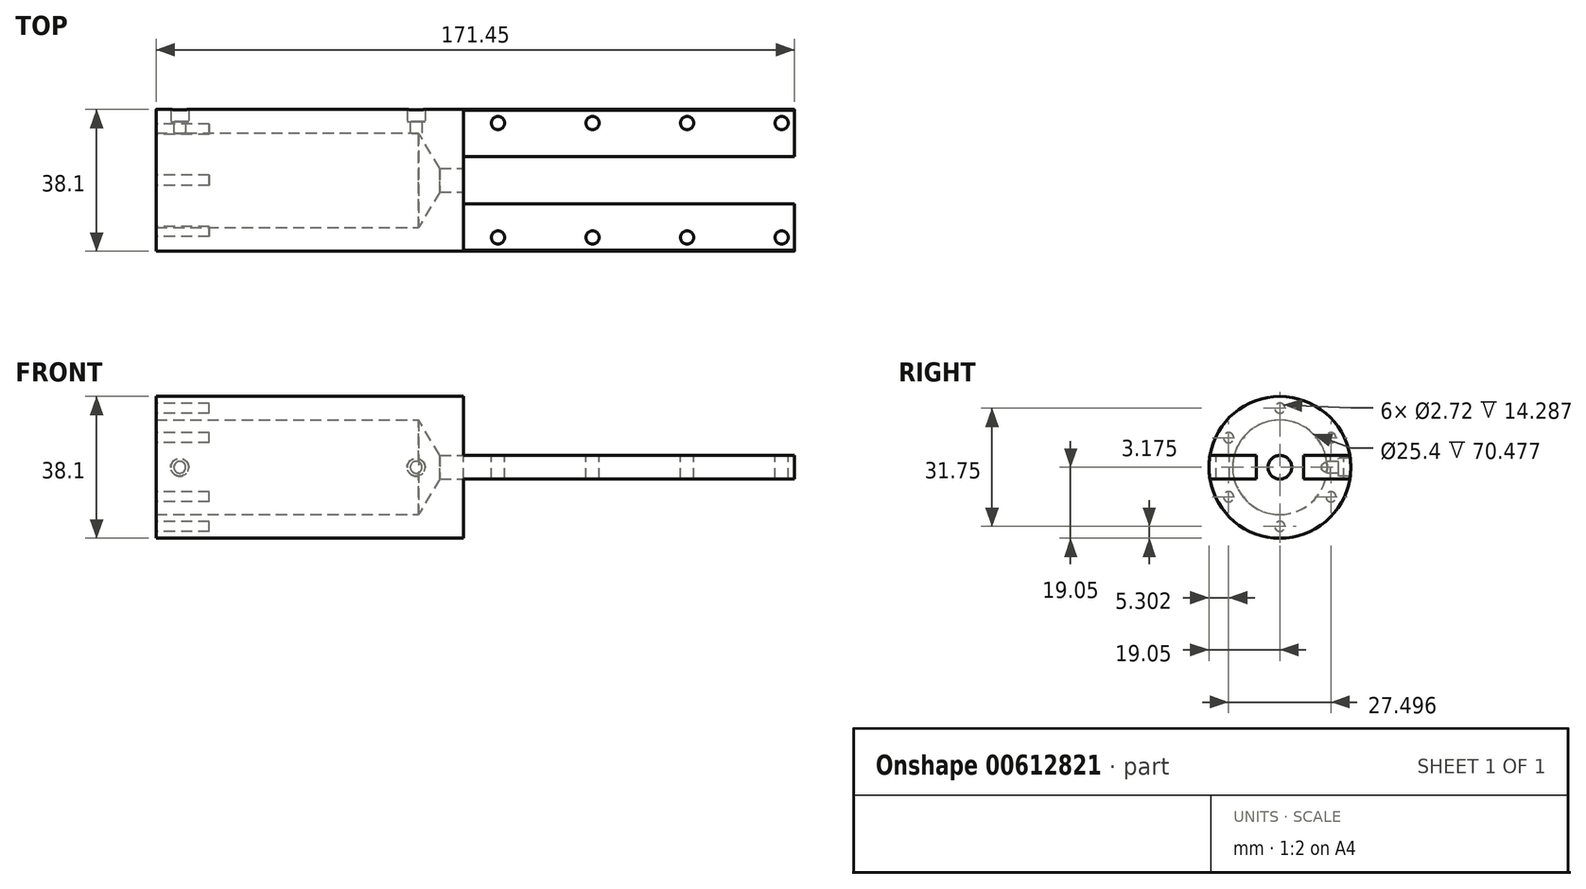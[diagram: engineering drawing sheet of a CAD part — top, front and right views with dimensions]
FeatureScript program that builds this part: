
annotation { "Feature Type Name" : "Feature", "Feature Type Description" : "" }
export const myFeature = defineFeature(function(context is Context, id is Id, definition is map)
    precondition{}
    {
        {
            var Q0;
            Q0=qCreatedBy(makeId("Right.planeOp"),FACE);
            var sketch = newSketch(context, id + "F0", { "sketchPlane" : qUnion([Q0])});
            skCircle(sketch, "E0", {"center": v(0, 0) * mm, "radius": 19.05 * mm});
            skSolve(sketch);
        }
        {
            var Q0;
            Q0=qSketchRegion(id+"F0",true);
            extrude(context, id + "F1", {"entities" : qUnion([Q0]), "depth" : 171.45 * mm});
        }
        {
            var Q0;
            Q0=qCreatedBy(makeId("Front.planeOp"),FACE);
            var sketch = newSketch(context, id + "F2", { "sketchPlane" : qUnion([Q0])});
            skLineSegment(sketch, "E1.bottom", {"start": v(82.55, 3.18) * mm, "end": v(171.45, 3.18) * mm});
            skLineSegment(sketch, "E1.top", {"start": v(82.55, 19.05) * mm, "end": v(171.45, 19.05) * mm});
            skLineSegment(sketch, "E1.left", {"start": v(82.55, 3.18) * mm, "end": v(82.55, 19.05) * mm});
            skLineSegment(sketch, "E1.right", {"start": v(171.45, 3.18) * mm, "end": v(171.45, 19.05) * mm});
            skLineSegment(sketch, "E2.bottom", {"start": v(82.55, -3.18) * mm, "end": v(171.45, -3.18) * mm});
            skLineSegment(sketch, "E2.top", {"start": v(82.55, -19.05) * mm, "end": v(171.45, -19.05) * mm});
            skLineSegment(sketch, "E2.left", {"start": v(82.55, -3.18) * mm, "end": v(82.55, -19.05) * mm});
            skLineSegment(sketch, "E2.right", {"start": v(171.45, -3.18) * mm, "end": v(171.45, -19.05) * mm});
            skLineSegment(sketch, "E3", {"start": v(0, 19.05) * mm, "end": v(171.45, 19.05) * mm, "construction": true});
            skLineSegment(sketch, "E4", {"start": v(171.45, -19.05) * mm, "end": v(0, -19.05) * mm, "construction": true});
            skSolve(sketch);
        }
        {
            var Q0;
            Q0=qSketchRegion(id+"F2",true);
            extrude(context, id + "F3", {"entities" : qUnion([Q0]), "operationType" : NewBodyOperationType.REMOVE, "oppositeDirection" : true, "depth" : 50.8 * mm, "symmetric" : true});
        }
        {
            var Q0;
            Q0=qCreatedBy(makeId("Top.planeOp"),FACE);
            var sketch = newSketch(context, id + "F4", { "sketchPlane" : qUnion([Q0])});
            skLineSegment(sketch, "E5.bottom", {"start": v(171.45, 6.35) * mm, "end": v(82.55, 6.35) * mm});
            skLineSegment(sketch, "E5.top", {"start": v(171.45, -6.35) * mm, "end": v(82.55, -6.35) * mm});
            skLineSegment(sketch, "E5.left", {"start": v(171.45, 6.35) * mm, "end": v(171.45, -6.35) * mm});
            skLineSegment(sketch, "E5.right", {"start": v(82.55, 6.35) * mm, "end": v(82.55, -6.35) * mm});
            skCircle(sketch, "E6", {"center": v(91.82, 15.37) * mm, "radius": 1.78 * mm});
            skCircle(sketch, "E7", {"center": v(91.82, -15.37) * mm, "radius": 1.78 * mm});
            skCircle(sketch, "E8.1.0.0", {"center": v(117.22, 15.37) * mm, "radius": 1.78 * mm});
            skCircle(sketch, "E8.1.0.1", {"center": v(117.22, -15.37) * mm, "radius": 1.78 * mm});
            skCircle(sketch, "E8.2.0.0", {"center": v(142.62, 15.37) * mm, "radius": 1.78 * mm});
            skCircle(sketch, "E8.2.0.1", {"center": v(142.62, -15.37) * mm, "radius": 1.78 * mm});
            skCircle(sketch, "E8.3.0.0", {"center": v(168.02, 15.37) * mm, "radius": 1.78 * mm});
            skCircle(sketch, "E8.3.0.1", {"center": v(168.02, -15.37) * mm, "radius": 1.78 * mm});
            skLineSegment(sketch, "E8.direction1", {"start": v(91.82, 15.37) * mm, "end": v(117.22, 15.37) * mm, "construction": true});
            skSolve(sketch);
        }
        {
            var Q0;
            Q0=qSketchRegion(id+"F4",true);
            extrude(context, id + "F5", {"entities" : qUnion([Q0]), "operationType" : NewBodyOperationType.REMOVE, "oppositeDirection" : true, "depth" : 50.8 * mm, "symmetric" : true});
        }
        {
            var Q0;
            Q0=qCreatedBy(makeId("Top.planeOp"),FACE);
            var sketch = newSketch(context, id + "F6", { "sketchPlane" : qUnion([Q0])});
            skLineSegment(sketch, "E9", {"start": v(0, 0) * mm, "end": v(82.55, 0) * mm});
            skLineSegment(sketch, "E10", {"start": v(82.55, 0) * mm, "end": v(82.55, 3.18) * mm});
            skLineSegment(sketch, "E11", {"start": v(82.55, 3.18) * mm, "end": v(76.2, 3.18) * mm});
            skLineSegment(sketch, "E12", {"start": v(76.2, 3.18) * mm, "end": v(70.48, 12.7) * mm});
            skLineSegment(sketch, "E13", {"start": v(70.48, 12.7) * mm, "end": v(0, 12.7) * mm});
            skLineSegment(sketch, "E14", {"start": v(0, 12.7) * mm, "end": v(0, 0) * mm});
            skSolve(sketch);
        }
        {
            var Q0;
            Q0=qSketchRegion(id+"F6",true);
            var Q1;
            Q1=sQuery(id+"F6.wireOp",EDGE,"E9");
            revolve(context, id + "F7", {"operationType" : NewBodyOperationType.REMOVE, "entities" : qUnion([Q0]), "axis" : qUnion([Q1]), "revolveType" : RevolveType.FULL, "oppositeDirection" : true});
        }
        {
            var Q0;
            Q0=qCreatedBy(makeId("Front.planeOp"),FACE);
            cPlane(context, id + "F8", {"entities" : qUnion([Q0]), "cplaneType" : CPlaneType.OFFSET, "offset" : 19.05 * mm, "oppositeDirection" : true, "width" : 152.4 * mm, "height" : 152.4 * mm});
        }
        {
            var Q0;
            Q0=qCreatedBy(id+"F8.planeOp",FACE);
            var sketch = newSketch(context, id + "F9", { "sketchPlane" : qUnion([Q0])});
            skPoint(sketch, "E15", {"position": v(6.35, 0) * mm});
            skPoint(sketch, "E16", {"position": v(69.85, 0) * mm});
            skSolve(sketch);
        }
        {
            var Q0;
            Q0=sQuery(id+"F9.wireOp",VERTEX,"E15");
            var Q1;
            Q1=sQuery(id+"F9.wireOp",VERTEX,"E16");
            var Q2;
            Q2=makeQuery(id+"F1.opExtrude","SWEPT_BODY",BODY,{"disambiguationData":[OSD([sQuery(id+"F0.wireOp",EDGE,"E0")])]});
            hole(context, id + "F10", {"style" : HoleStyle.C_BORE, "holeDiameter" : 3.17 * mm, "cBoreDiameter" : 4.78 * mm, "cBoreDepth" : 3.17 * mm, "endStyle" : HoleEndStyle.BLIND, "oppositeDirection" : true, "holeDepth" : 7.62 * mm, "locations" : qUnion([Q0, Q1]), "scope" : qUnion([Q2])});
        }
        {
            var Q0;
            Q0=qCreatedBy(makeId("Right.planeOp"),FACE);
            var sketch = newSketch(context, id + "F11", { "sketchPlane" : qUnion([Q0])});
            skCircle(sketch, "E17", {"center": v(0, 0) * mm, "radius": 15.88 * mm, "construction": true});
            skCircle(sketch, "E18", {"center": v(0, 15.88) * mm, "radius": 1.36 * mm});
            skCircle(sketch, "E19.1.0", {"center": v(-13.75, 7.94) * mm, "radius": 1.36 * mm});
            skCircle(sketch, "E19.2.0", {"center": v(-13.75, -7.94) * mm, "radius": 1.36 * mm});
            skCircle(sketch, "E19.3.0", {"center": v(0, -15.88) * mm, "radius": 1.36 * mm});
            skCircle(sketch, "E19.4.0", {"center": v(13.75, -7.94) * mm, "radius": 1.36 * mm});
            skCircle(sketch, "E19.5.0", {"center": v(13.75, 7.94) * mm, "radius": 1.36 * mm});
            skLineSegment(sketch, "E20", {"start": v(0, 0) * mm, "end": v(0, 15.88) * mm, "construction": true});
            skSolve(sketch);
        }
        {
            var Q0;
            Q0=qSketchRegion(id+"F11",true);
            extrude(context, id + "F12", {"entities" : qUnion([Q0]), "operationType" : NewBodyOperationType.REMOVE, "depth" : 14.29 * mm});
        }
    });
